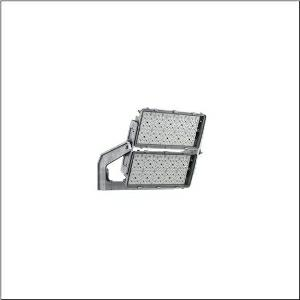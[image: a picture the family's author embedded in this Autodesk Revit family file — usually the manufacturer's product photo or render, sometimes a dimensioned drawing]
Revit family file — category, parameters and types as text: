
# Revit family: floodlight_fl_11_maxi_remote___rs07_5xa779514k01aa_47cf
name_source: partatom
category: Lighting Fixtures
units: mm (PartAtom-declared; Revit-internal decimal feet)

## family parameters
Cut with Voids When Loaded = No
Host = Face
Light Source = No
Part Type = Normal
Room Calculation Point = No
Round Connector Dimension = Use Diameter
Shared = No

## types (1)
- --- (1 x LED, 88570 lm, 916.8 W, 5700K)
    Apparent Load = 917 VA
    CIE Flux Codes = 80 93 99 100 99
    Color Rendering = 90
    Color Temperature = 5700K
    Default Elevation = 1800 mm
    Description = Floodlight FL 11  maxi  Remote floodlight; light control with lens of PMMA; cover panel of toughened safety glass, transparent; light distribution: RS07, rotationally symmetric direct distribution, LEDcolour temperature: 5700K, rated luminous flux: 88.570lm, colour rendering: CRI > 90, light colour: 957; luminous efficacy: 97lm/W; brightness control: DMX+RDM; with terminal, 6-pole, max. 2.5mm², mains connection: 220..240V/380..400V AC, 50/60Hz, surge voltage resistance: line to ground: 10kV, ECG replaceable separately, no afterglow with DALI off / DMX off command, LED unit replaceable without ESD environment, dustproof LED module, dimming range 10..100%; 917W floodlight with 2x LED unit of diecast aluminium, coated grey; length: 713mm / width: 651mm / height: 338mm; mounting bracket, of diecast aluminium, uncoated, natural, equipment: Power, protection rating (complete): IP66; insulation class (complete): insulation class I (protective earthing); certification: CE, ENEC, VDE; ball protection: ball impact resistance with accessories, impact resistance: IK07; rated ambient temperature 10°C, only for outdoor installations, permissible operating ambient temperature: -40..+30°C, permissible storage temperature: -40..+85°Cpackaging unit: 1 piece

Light Distribution: RS07
    Height = 320 mm
    Lamp = 1 x LED
    Lamp Light Flux = 88570 lm
    Lamp Power = 916.8 W
    Lamp count = 1
    Length = 712 mm
    Luminous efficacy = 97 lm/W
    Manufacturer = Siteco
    ModVariant = No
    Model = 5XA779514K01AA
    Mounting Place = Ceiling
    Mounting Type = Surface mounted
    Number of Poles = 1
    OnlyDefault = Yes
    Power Factor = 1
    Product Name = Floodlight FL 11 maxi Remote | RS07
    Product group = floodlight | ceiling mounted
    ProductGroupID = 301
    Protection Class = Protection class I
    Protection Degree = IP 66
    RLX_Detail_Level = 1
    RLX_Emergency_Light_Flux = 0 lm
    RLX_Emergency_Type = 0
    RLX_Emergency_Type_DB = No
    RlxData = <blob elided: 41093 chars, md5=8ea8a62e>
    Socket = socket
    Standby Power = 0 W
    System Light Flux = 88570 lm
    System Power = 917 W
    Type Comments = factory setting: luminous flux: 100 % | dim-lin: 254 | 950 mA
    Type Image = l_1349125.jpg
    URL = http://relux.com
    VarID = @adj_181450
    Voltage = 0 V
    Weight = 0.00 kg
    Width = 655 mm

## geometry (parser evidence)
native form markers: Blend x4, Sweep x11
no freeform markers — native parametric forms only
